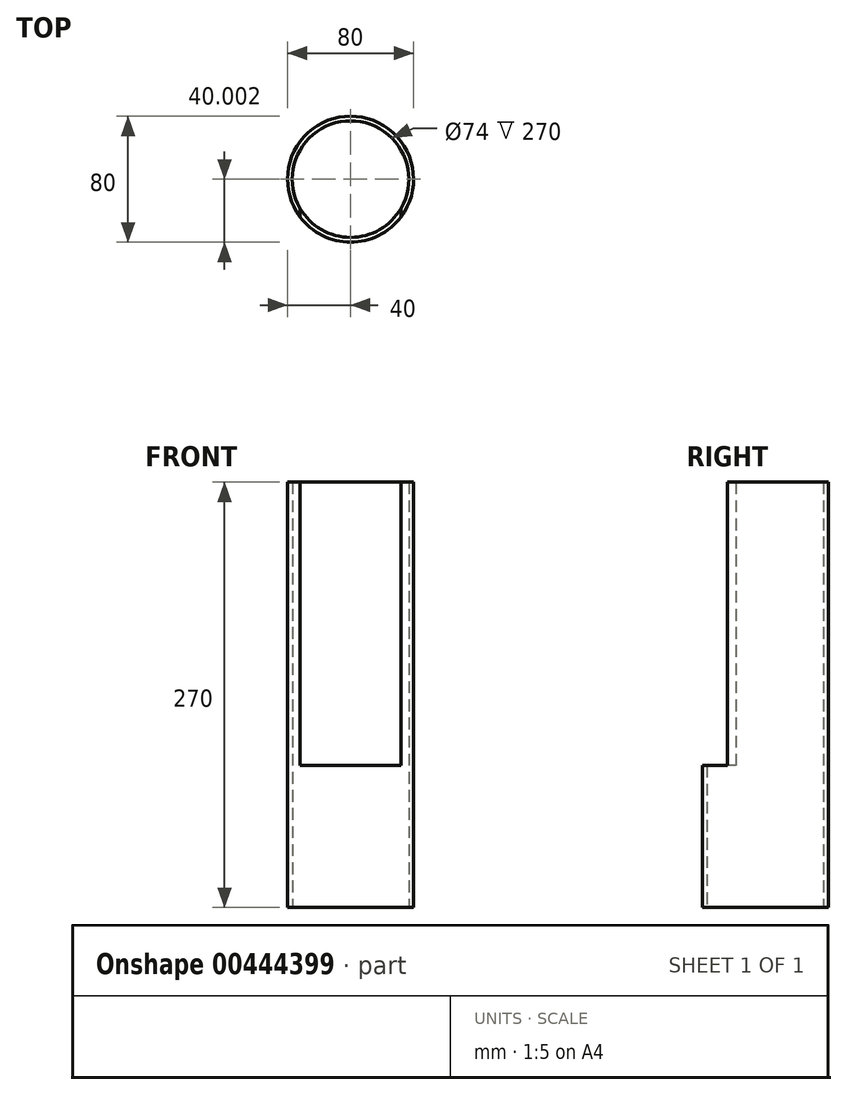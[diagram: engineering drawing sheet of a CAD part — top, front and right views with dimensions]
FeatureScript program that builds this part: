
annotation { "Feature Type Name" : "Feature", "Feature Type Description" : "" }
export const myFeature = defineFeature(function(context is Context, id is Id, definition is map)
    precondition{}
    {
        {
            var Q0;
            Q0=qCreatedBy(makeId("Top.planeOp"),FACE);
            var sketch = newSketch(context, id + "F0", { "sketchPlane" : qUnion([Q0])});
            skCircle(sketch, "E0", {"center": v(0, 2.37) * mm, "radius": 40 * mm});
            skCircle(sketch, "E1", {"center": v(0, 2.37) * mm, "radius": 37 * mm});
            skSolve(sketch);
        }
        {
            var Q0;
            Q0 = qSketchRegion(id + "F0", true);
            extrude(context, id + "F1", {"entities" : qUnion([Q0]), "depth" : 270 * mm});
        }
        {
            var Q0;
            Q0=makeQuery(id+"F1.opExtrude","CAP_FACE",FACE,{"disambiguationData":[OSD([sQuery(id+"F0.wireOp",EDGE,"E0"),sQuery(id+"F0.wireOp",EDGE,"E1")])],"isStart":false});
            var sketch = newSketch(context, id + "F2", { "sketchPlane" : qUnion([Q0])});
            skLineSegment(sketch, "E2.bottom", {"start": v(0, 0) * mm, "end": v(32, 0) * mm});
            skLineSegment(sketch, "E2.top", {"start": v(0, -84.36) * mm, "end": v(32, -84.36) * mm});
            skLineSegment(sketch, "E2.right", {"start": v(32, 0) * mm, "end": v(32, -84.36) * mm});
            skLineSegment(sketch, "E3.MirrorCS", {"start": v(32, 0) * mm, "end": v(32, 84.36) * mm});
            skLineSegment(sketch, "E4.MirrorCS", {"start": v(0, 84.36) * mm, "end": v(32, 84.36) * mm});
            skLineSegment(sketch, "E5.MirrorCS", {"start": v(0, 0) * mm, "end": v(-32, 0) * mm});
            skLineSegment(sketch, "E6.MirrorCS", {"start": v(-32, 0) * mm, "end": v(-32, -84.36) * mm});
            skLineSegment(sketch, "E7.MirrorCS", {"start": v(0, -84.36) * mm, "end": v(-32, -84.36) * mm});
            skSolve(sketch);
        }
        {
            var Q0;
            Q0 = qSketchRegion(id + "F2", true);
            extrude(context, id + "F3", {"entities" : qUnion([Q0]), "operationType" : NewBodyOperationType.REMOVE, "oppositeDirection" : true, "depth" : 180 * mm});
        }
    });
